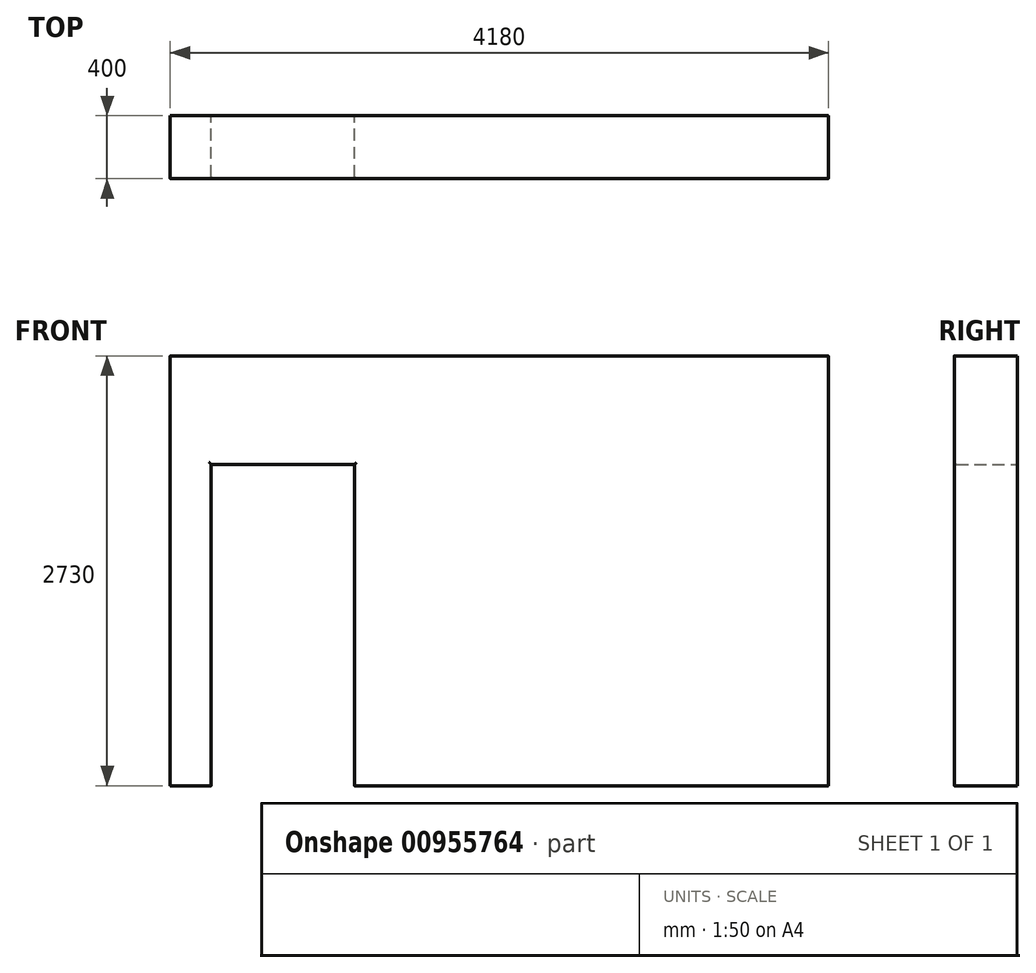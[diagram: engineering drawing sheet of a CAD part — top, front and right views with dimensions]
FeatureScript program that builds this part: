
annotation { "Feature Type Name" : "Feature", "Feature Type Description" : "" }
export const myFeature = defineFeature(function(context is Context, id is Id, definition is map)
    precondition{}
    {
        {
            var Q0;
            Q0=qCreatedBy(makeId("Front.planeOp"),FACE);
            var sketch = newSketch(context, id + "F0", { "sketchPlane" : qUnion([Q0])});
            skLineSegment(sketch, "E0.bottom", {"start": v(-2083.35, 2730) * mm, "end": v(2096.65, 2730) * mm});
            skLineSegment(sketch, "E0.top", {"start": v(-2083.35, 0) * mm, "end": v(2096.65, 0) * mm});
            skLineSegment(sketch, "E0.left", {"start": v(-2083.35, 2730) * mm, "end": v(-2083.35, 0) * mm});
            skLineSegment(sketch, "E0.right", {"start": v(2096.65, 2730) * mm, "end": v(2096.65, 0) * mm});
            skLineSegment(sketch, "E1", {"start": v(-2083.35, 0) * mm, "end": v(-1823.35, 0) * mm});
            skLineSegment(sketch, "E2", {"start": v(-1823.35, 0) * mm, "end": v(-1823.35, 2040) * mm});
            skLineSegment(sketch, "E3", {"start": v(-1823.35, 2040) * mm, "end": v(-913.35, 2040) * mm});
            skLineSegment(sketch, "E4", {"start": v(-913.35, 2040) * mm, "end": v(-913.35, 0) * mm});
            skSolve(sketch);
        }
        {
            var Q0;
            Q0=makeQuery(id+"F0.imprint","IMPRINT",FACE,{"disambiguationData":[TD([[makeQuery(id+"F0.imprint","IMPRINT",EDGE,{"derivedFrom":sQuery(id+"F0.wireOp",EDGE,"E0.bottom")}),-1.0]])]});
            extrude(context, id + "F1", {"entities" : qUnion([Q0]), "depth" : 400 * mm, "offsetDistance" : 25.4 * mm});
        }
        {
            var Q0;
            Q0=makeQuery(id+"F1.opExtrude","CAP_EDGE",EDGE,{"disambiguationData":[OSD([sQuery(id+"F0.wireOp",EDGE,"E2")])],"isStart":false});
            fillet(context, id + "F2", {"entities" : qUnion([Q0]), "radius" : 12.7 * mm, "tangentPropagation" : true, "allowEdgeOverflow" : false});
        }
        {
            var Q0;
            Q0=makeQuery(id+"F1.opExtrude","CAP_EDGE",EDGE,{"disambiguationData":[OSD([sQuery(id+"F0.wireOp",EDGE,"E4")])],"isStart":false});
            fillet(context, id + "F3", {"entities" : qUnion([Q0]), "radius" : 12.7 * mm, "tangentPropagation" : true, "allowEdgeOverflow" : false});
        }
        {
            var Q0;
            Q0=makeQuery(id+"F1.opExtrude","CAP_EDGE",EDGE,{"disambiguationData":[OSD([sQuery(id+"F0.wireOp",EDGE,"E3")])],"isStart":false});
            fillet(context, id + "F4", {"entities" : qUnion([Q0]), "radius" : 12.7 * mm, "tangentPropagation" : true, "allowEdgeOverflow" : false});
        }
        {
            var Q0;
            {var subQ0=sQuery(id+"F0.wireOp",EDGE,"E0.top");Q0=makeQuery(id+"F1.opExtrude","CAP_EDGE",EDGE,{"disambiguationData":[OSD([subQ0]),TDD([makeQuery(id+"F0.imprint","IMPRINT",EDGE,{"disambiguationData":[TD([[makeQuery(id+"F0.imprint","INTERSECT",VERTEX,{"derivedFrom":[subQ0,sQuery(id+"F0.wireOp",EDGE,"E2")]}),1.0]])],"derivedFrom":subQ0})])],"isStart":false});}
            var Q1;
            {var subQ0=sQuery(id+"F0.wireOp",EDGE,"E0.top");Q1=makeQuery(id+"F1.opExtrude","CAP_EDGE",EDGE,{"disambiguationData":[OSD([subQ0]),TDD([makeQuery(id+"F0.imprint","IMPRINT",EDGE,{"disambiguationData":[TD([[makeQuery(id+"F0.imprint","INTERSECT",VERTEX,{"derivedFrom":[subQ0,sQuery(id+"F0.wireOp",EDGE,"E4")]}),-1.0]])],"derivedFrom":subQ0})])],"isStart":false});}
            fillet(context, id + "F5", {"entities" : qUnion([Q0, Q1]), "radius" : ((0.5 * sqrt(2)) / 2) * mm, "tangentPropagation" : true, "allowEdgeOverflow" : false});
        }
        {
            var Q0;
            Q0=makeQuery(id+"F1.opExtrude","CAP_EDGE",EDGE,{"disambiguationData":[OSD([sQuery(id+"F0.wireOp",EDGE,"E0.left")])],"isStart":false});
            fillet(context, id + "F6", {"entities" : qUnion([Q0]), "radius" : ((.5 * sqrt(2)) / 2) * mm, "tangentPropagation" : true, "allowEdgeOverflow" : false});
        }
        {
            var Q0;
            Q0=makeQuery(id+"F1.opExtrude","CAP_EDGE",EDGE,{"disambiguationData":[OSD([sQuery(id+"F0.wireOp",EDGE,"E0.right")])],"isStart":false});
            fillet(context, id + "F7", {"entities" : qUnion([Q0]), "radius" : ((.5 * sqrt(2)) / 2) * mm, "tangentPropagation" : true, "allowEdgeOverflow" : false});
        }
        {
            var Q0;
            Q0=makeQuery(id+"F1.opExtrude","CAP_EDGE",EDGE,{"disambiguationData":[OSD([sQuery(id+"F0.wireOp",EDGE,"E0.bottom")])],"isStart":false});
            fillet(context, id + "F8", {"entities" : qUnion([Q0]), "radius" : ((.5 * sqrt(2)) / 2) * mm, "tangentPropagation" : true, "allowEdgeOverflow" : false});
        }
    });
